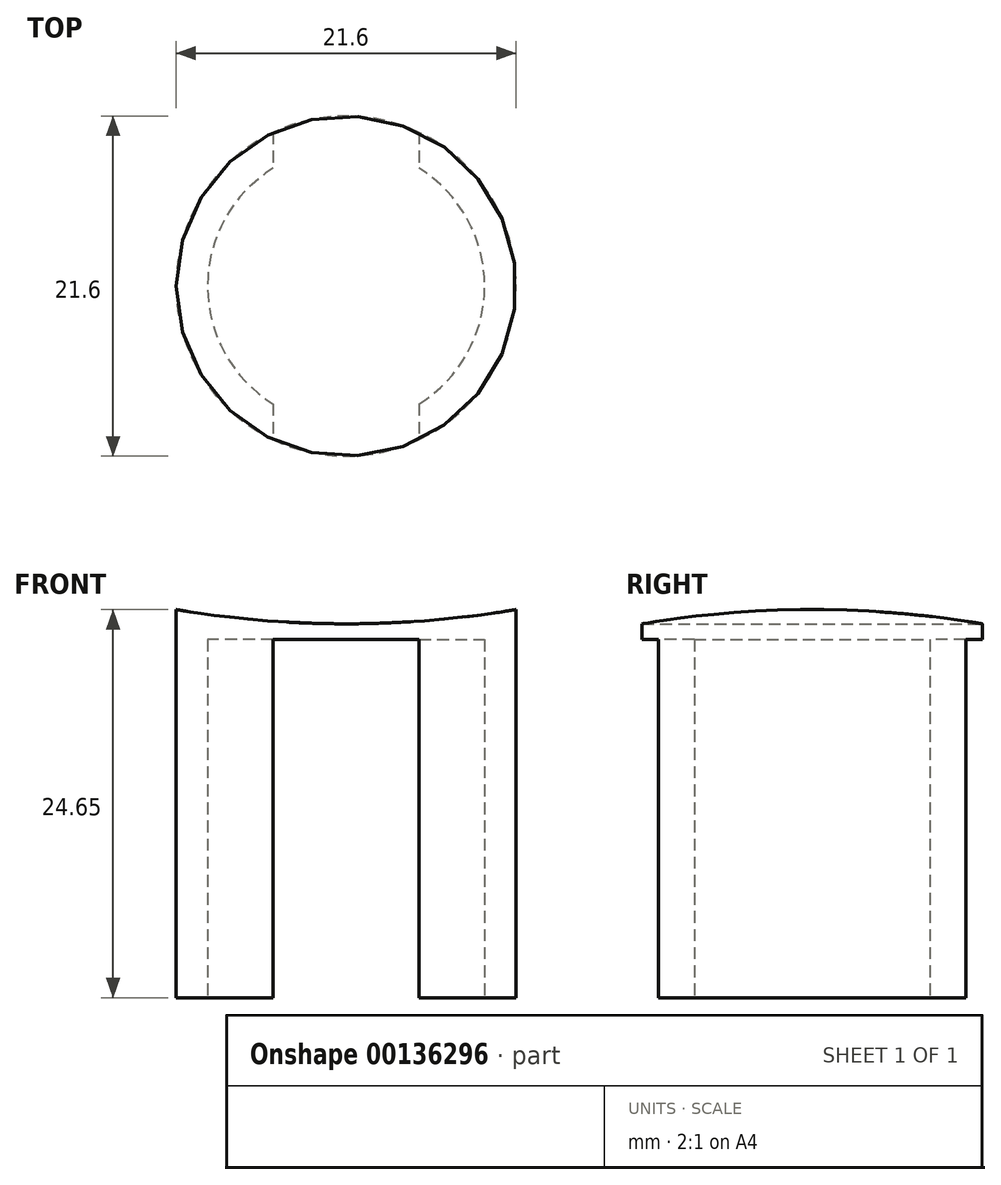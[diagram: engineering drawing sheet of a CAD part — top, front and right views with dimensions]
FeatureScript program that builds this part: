
annotation { "Feature Type Name" : "Feature", "Feature Type Description" : "" }
export const myFeature = defineFeature(function(context is Context, id is Id, definition is map)
    precondition{}
    {
        {
            var Q0;
            Q0=qCreatedBy(makeId("Front.planeOp"),FACE);
            var sketch = newSketch(context, id + "F0", { "sketchPlane" : qUnion([Q0])});
            skLineSegment(sketch, "E0.left", {"start": v(10.8, 15.25) * mm, "end": v(10.8, -12.5) * mm});
            skLineSegment(sketch, "E1.left", {"start": v(8.8, 10.25) * mm, "end": v(8.8, -11.75) * mm});
            skLineSegment(sketch, "E2", {"start": v(10.8, -12.5) * mm, "end": v(8.8, -12.5) * mm});
            skLineSegment(sketch, "E3", {"start": v(8.8, -12.5) * mm, "end": v(8.8, -11.75) * mm});
            skLineSegment(sketch, "E4", {"start": v(0, 9.11) * mm, "end": v(0, 15.25) * mm});
            skLineSegment(sketch, "E5", {"start": v(8.8, 10.25) * mm, "end": v(0, 10.25) * mm});
            skLineSegment(sketch, "E6", {"start": v(10.8, 15.25) * mm, "end": v(0, 15.25) * mm});
            skSolve(sketch);
        }
        {
            var Q0;
            {var subQ5=sQuery(id+"F0.wireOp",EDGE,"E0.left");Q0=makeQuery(id+"F0.imprint","IMPRINT",FACE,{"disambiguationData":[TD([[makeQuery(id+"F0.imprint","IMPRINT",EDGE,{"derivedFrom":subQ5}),-1.0]])]});}
            var Q1;
            Q1=sQuery(id+"F0.wireOp",EDGE,"E4");
            revolve(context, id + "F1", {"entities" : qUnion([Q0]), "axis" : qUnion([Q1]), "revolveType" : RevolveType.FULL});
        }
        {
            var Q0;
            Q0=makeQuery(id+"F1.opRevolve","SWEPT_FACE",FACE,{"disambiguationData":[OSD([sQuery(id+"F0.wireOp",EDGE,"E2")])]});
            var sketch = newSketch(context, id + "F2", { "sketchPlane" : qUnion([Q0])});
            skLineSegment(sketch, "E7.bottom", {"start": v(4.64, -11.75) * mm, "end": v(-4.64, -11.75) * mm});
            skLineSegment(sketch, "E7.top", {"start": v(4.64, 11.75) * mm, "end": v(-4.64, 11.75) * mm});
            skLineSegment(sketch, "E7.left", {"start": v(4.64, -11.75) * mm, "end": v(4.64, 11.75) * mm});
            skLineSegment(sketch, "E7.right", {"start": v(-4.64, -11.75) * mm, "end": v(-4.64, 11.75) * mm});
            skPoint(sketch, "E7.middle", {"position": v(0, 0) * mm});
            skSolve(sketch);
        }
        {
            var Q0;
            Q0 = qSketchRegion(id + "F2", true);
            var Q1;
            Q1=makeQuery(id+"F1.opRevolve","SWEPT_FACE",FACE,{"disambiguationData":[OSD([sQuery(id+"F0.wireOp",EDGE,"E5")])]});
            extrude(context, id + "F3", {"entities" : qUnion([Q0]), "operationType" : NewBodyOperationType.REMOVE, "endBound" : BoundingType.UP_TO_SURFACE, "oppositeDirection" : true, "endBoundEntityFace" : qUnion([Q1]), "depth" : 20 * mm});
        }
        {
            var Q0;
            Q0=qCreatedBy(makeId("Front.planeOp"),FACE);
            var sketch = newSketch(context, id + "F4", { "sketchPlane" : qUnion([Q0])});
            skLineSegment(sketch, "E8.0", {"start": v(-4.64, 10.25) * mm, "end": v(4.64, 10.25) * mm, "construction": true});
            skCircle(sketch, "E9", {"center": v(0, 76.25) * mm, "radius": 65 * mm});
            skPoint(sketch, "E9.centerSnap0", {"position": v(0, 10.25) * mm});
            skSolve(sketch);
        }
        {
            var Q0;
            Q0 = qSketchRegion(id + "F4", true);
            extrude(context, id + "F5", {"entities" : qUnion([Q0]), "operationType" : NewBodyOperationType.REMOVE, "endBound" : BoundingType.SYMMETRIC, "depth" : 25 * mm});
        }
    });
